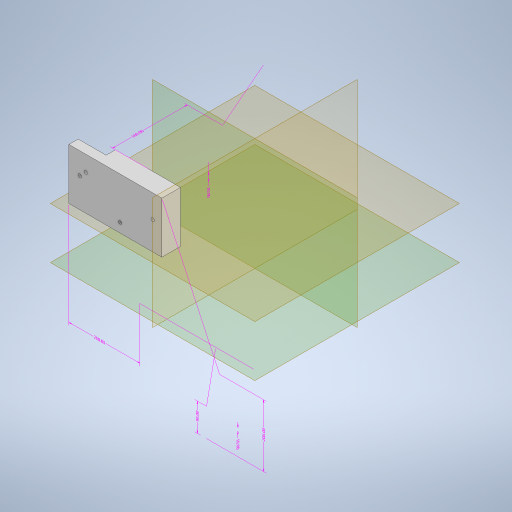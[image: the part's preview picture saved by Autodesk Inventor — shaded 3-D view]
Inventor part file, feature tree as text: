
AUTODESK INVENTOR PART (.ipt)
format: ipt  version: 2023 (Build 270158000, 158)  size: 446,464 bytes
history: native  units: mm
features: other x9, sketch x9, extrude x5, hole x4, plane x4, split x3
ambient origin geometry x8: Origin, YZ Plane, XZ Plane, XY Plane, X Axis, Y Axis, Z Axis, Center Point
bodies: Body1 (feature_tree)
feature tree (34):
  other  "Sólido1"
  other  "Anotaciones"
  extrude  "Extrusión1"  Depth=200.0mm
  hole  "Agujero1"  [1 undecoded]
  extrude  "Extrusión2"  Depth=15.0mm
  extrude  "Extrusión3"  Depth=20.0mm TaperAngle=0.0deg
  extrude  "Extrusión4"  Depth=200.0mm
  extrude  "Extrusión5"  Depth=20.0mm
  hole  "Agujero2"  [1 undecoded]
  plane  "Plano de trabajo1"
  split  "Dividir1"
  plane  "Plano de trabajo2"
  plane  "Plano de trabajo3"
  plane  "Plano de trabajo4"
  hole  "Agujero3"  [1 undecoded]
  hole  "Agujero4"  [1 undecoded]
  split  "Dividir2"
  split  "Dividir3"
  other  "Suprimir cara5"
  sketch  "Boceto2"  dims[d7=15.0mm d8=200.0mm]
  sketch  "Boceto3"  dims[d9=10.0mm d10=0.0mm]
  sketch  "Boceto4"  dims[d11=3.5mm d12=1.75mm d13=1.75mm d14=1.75mm d15=1.75mm d16=10.0mm d17=10.0mm d19=40.0mm]
  sketch  "Boceto5"  dims[d20=3.5mm d21=6.0mm d22=4.0mm d23=2.0mm d24=90.0deg d25=8.0mm d26=20.594885mm d27=15.0mm]
  sketch  "Boceto6"  dims[d28=20.0mm d29=80.0mm d30=0.0mm]
  sketch  "Boceto7"  dims[d31=57.0mm d32=200.0mm]
  sketch  "Boceto8"  dims[d33=110.0mm d34=0.0mm d36=20.0mm]
  sketch  "Boceto9"  dims[d37=20.0mm d38=20.0mm]
  sketch  "Boceto10"  dims[d39=90.0mm d40=0.0mm d43=30.0mm d44=0.0mm d45=3.5mm d46=1.75mm d47=1.75mm d48=1.75mm d49=1.75mm d50=10.0mm d51=10.0mm d52=15.0mm d53=10.0mm d54=10.0mm d55=15.0mm d56=3.5mm d57=6.0mm d58=4.0mm d59=2.0mm d60=90.0deg d61=8.0mm d62=20.594885mm d63=10.0mm d65=10.0mm d75=200.0mm d76=10.0mm d77=20.0mm d81=40.0mm d88=90.0deg d89=10.0mm d90=30.0mm d91=5.0mm d92=5.0mm d93=5.0mm d94=5.0mm d95=30.0mm d96=5.0mm d97=5.0mm d98=3.5mm d99=5.0mm d100=5.0mm d101=5.0mm d102=5.0mm d103=5.0mm d104=20.0mm d105=3.5mm d106=6.0mm d107=4.0mm d108=2.0mm d109=90.0deg d110=8.0mm d111=20.594885mm d112=10.0mm d113=30.0mm d114=5.0mm d115=5.0mm d116=5.0mm d117=5.0mm d118=5.0mm d119=5.0mm d120=3.5mm d121=5.0mm d122=5.0mm d123=5.0mm d124=5.0mm d125=5.0mm d126=30.0mm d127=30.0mm d128=3.5mm d129=6.0mm d130=4.0mm d131=2.0mm d132=90.0deg d133=8.0mm d134=20.594885mm d66=5.760865mm d67=7.72461mm d68=200.0mm d69=3.008686mm d70=2.422102mm d71=10.0mm d72=3.500509mm d73=2.402572mm d74=90.0mm d78=3.13122mm d79=6.269346mm d80=200.0mm d82=8.450127mm d83=0.968417mm d84=20.0mm d85=4.759975mm d86=4.646891mm d87=160.0mm]
  other  "Cota lineal 1"
  other  "Cota lineal 2"
  other  "Cota lineal 3"
  other  "Cota lineal 4"
  other  "Cota lineal 5"
  other  "Cota lineal 6"
note: 4 required parameter values undecoded (feature->parameter linkage not recoverable at this tier; creation-order binding heuristic only, values carry confidence <= 0.55)
